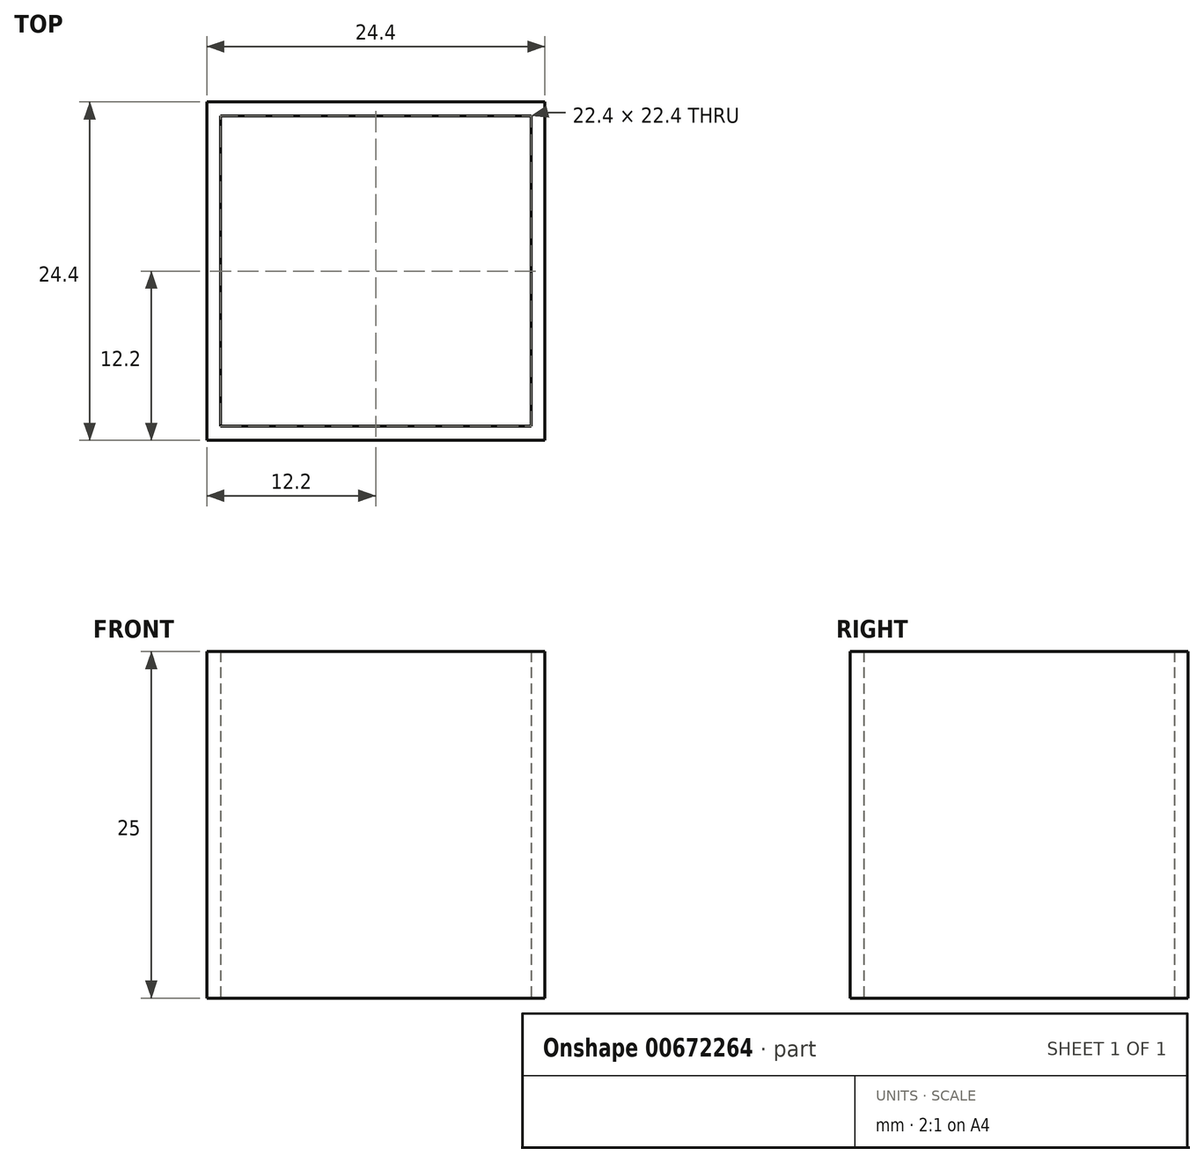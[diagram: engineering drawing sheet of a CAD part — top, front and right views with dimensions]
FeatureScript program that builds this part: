
annotation { "Feature Type Name" : "Feature", "Feature Type Description" : "" }
export const myFeature = defineFeature(function(context is Context, id is Id, definition is map)
    precondition{}
    {
        {
            var Q0;
            Q0=qCreatedBy(makeId("Top.planeOp"),FACE);
            var sketch = newSketch(context, id + "F0", { "sketchPlane" : qUnion([Q0])});
            skLineSegment(sketch, "E0.top", {"start": v(-11.2, -11.2) * mm, "end": v(11.2, -11.2) * mm});
            skLineSegment(sketch, "E0.left", {"start": v(-11.2, 11.2) * mm, "end": v(-11.2, -11.2) * mm});
            skLineSegment(sketch, "E1", {"start": v(-11.2, 11.2) * mm, "end": v(0, 11.2) * mm});
            skLineSegment(sketch, "E2", {"start": v(0, 11.2) * mm, "end": v(11.2, 11.2) * mm});
            skLineSegment(sketch, "E3", {"start": v(11.2, 11.2) * mm, "end": v(11.2, 0) * mm});
            skLineSegment(sketch, "E4", {"start": v(11.2, 0) * mm, "end": v(11.2, -11.2) * mm});
            skLineSegment(sketch, "E5.0", {"start": v(-12.2, 12.2) * mm, "end": v(-12.2, -12.2) * mm});
            skLineSegment(sketch, "E5.1", {"start": v(0.01, 12.2) * mm, "end": v(12.2, 12.2) * mm});
            skLineSegment(sketch, "E5.2", {"start": v(12.2, 12.2) * mm, "end": v(12.2, -0.1) * mm});
            skLineSegment(sketch, "E5.3", {"start": v(-12.2, 12.2) * mm, "end": v(0.01, 12.2) * mm});
            skLineSegment(sketch, "E5.4", {"start": v(12.2, -0.1) * mm, "end": v(12.2, -12.2) * mm});
            skLineSegment(sketch, "E5.5", {"start": v(-12.2, -12.2) * mm, "end": v(12.2, -12.2) * mm});
            skSolve(sketch);
        }
        {
            var Q0;
            Q0 = qSketchRegion(id + "F0", true);
            extrude(context, id + "F1", {"entities" : qUnion([Q0]), "endBound" : BoundingType.SYMMETRIC, "depth" : 25 * mm, "offsetDistance" : 25 * mm, "hasSecondDirection" : true, "secondDirectionOppositeDirection" : true, "secondDirectionDepth" : 25 * mm});
        }
    });
